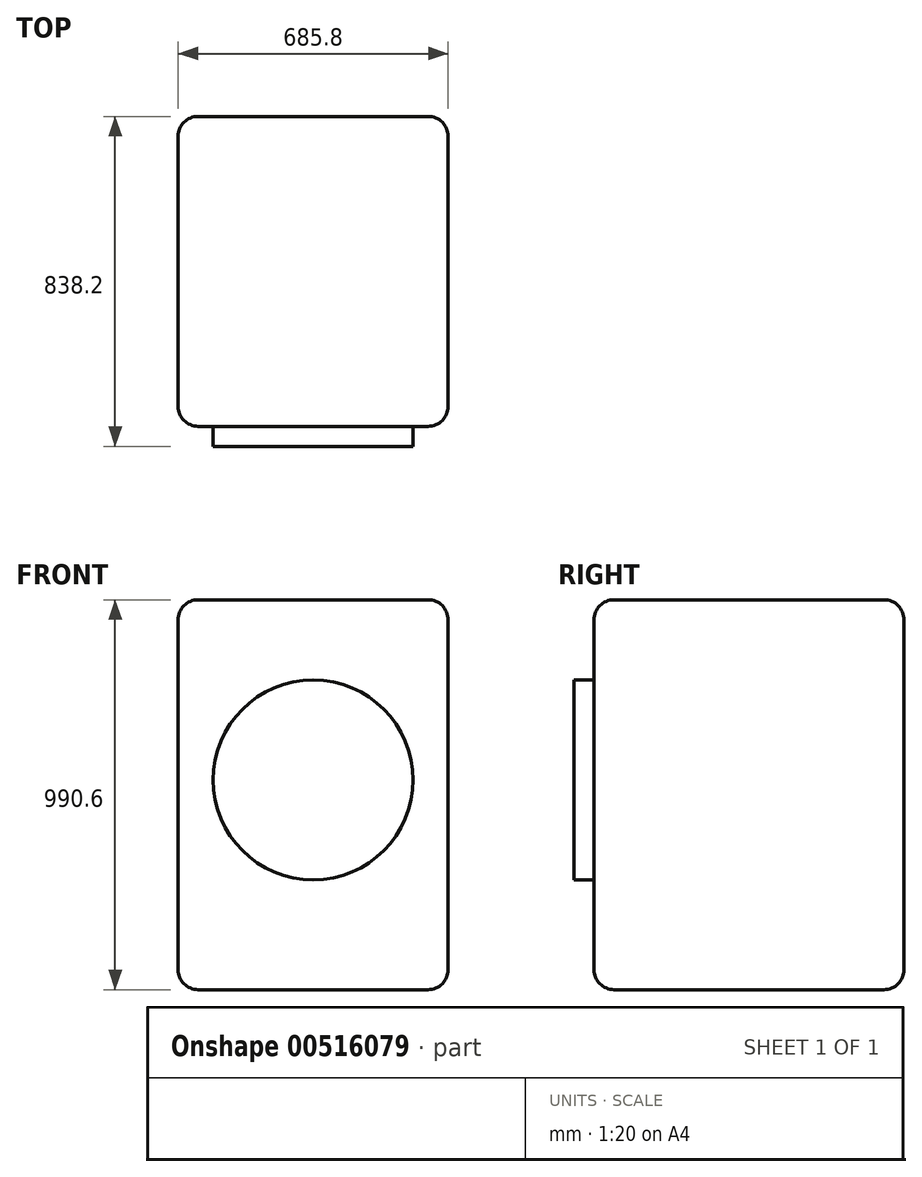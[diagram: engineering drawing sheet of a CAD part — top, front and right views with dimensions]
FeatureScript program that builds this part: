
annotation { "Feature Type Name" : "Feature", "Feature Type Description" : "" }
export const myFeature = defineFeature(function(context is Context, id is Id, definition is map)
    precondition{}
    {
        {
            var Q0;
            Q0=qCreatedBy(makeId("Top.planeOp"),FACE);
            var sketch = newSketch(context, id + "F0", { "sketchPlane" : qUnion([Q0])});
            skLineSegment(sketch, "E0.bottom", {"start": v(342.9, -393.7) * mm, "end": v(-342.9, -393.7) * mm});
            skLineSegment(sketch, "E0.top", {"start": v(342.9, 393.7) * mm, "end": v(-342.9, 393.7) * mm});
            skLineSegment(sketch, "E0.left", {"start": v(342.9, -393.7) * mm, "end": v(342.9, 393.7) * mm});
            skLineSegment(sketch, "E0.right", {"start": v(-342.9, -393.7) * mm, "end": v(-342.9, 393.7) * mm});
            skPoint(sketch, "E0.middle", {"position": v(0, 0) * mm});
            skSolve(sketch);
        }
        {
            var Q0;
            Q0=makeQuery(id+"F0.imprint","IMPRINT",FACE,{"disambiguationData":[TD([[makeQuery(id+"F0.imprint","IMPRINT",EDGE,{"derivedFrom":sQuery(id+"F0.wireOp",EDGE,"E0.bottom")}),-1.0]])]});
            extrude(context, id + "F1", {"entities" : qUnion([Q0]), "depth" : 990.6 * mm, "offsetDistance" : 25.4 * mm});
        }
        {
            var Q0;
            Q0=makeQuery(id+"F1.opExtrude","SWEPT_FACE",FACE,{"disambiguationData":[OSD([sQuery(id+"F0.wireOp",EDGE,"E0.bottom")])]});
            var sketch = newSketch(context, id + "F2", { "sketchPlane" : qUnion([Q0])});
            skCircle(sketch, "E1", {"center": v(0, 532.9) * mm, "radius": 253.93 * mm});
            skSolve(sketch);
        }
        {
            var Q0;
            Q0=makeQuery(id+"F2.imprint","IMPRINT",FACE,{"disambiguationData":[TD([[makeQuery(id+"F2.imprint","IMPRINT",EDGE,{"derivedFrom":sQuery(id+"F2.wireOp",EDGE,"E1")}),1.0]])]});
            extrude(context, id + "F3", {"entities" : qUnion([Q0]), "operationType" : NewBodyOperationType.ADD, "depth" : 50.8 * mm, "offsetDistance" : 25.4 * mm});
        }
        {
            var Q0;
            Q0=makeQuery(id+"F1.opExtrude","SWEPT_EDGE",EDGE,{"disambiguationData":[OSD([sQuery(id+"F0.wireOp",EDGE,"E0.bottom"),sQuery(id+"F0.wireOp",EDGE,"E0.right")])]});
            var Q1;
            Q1=makeQuery(id+"F1.opExtrude","CAP_EDGE",EDGE,{"disambiguationData":[OSD([sQuery(id+"F0.wireOp",EDGE,"E0.bottom")])],"isStart":false});
            var Q2;
            Q2=makeQuery(id+"F1.opExtrude","SWEPT_EDGE",EDGE,{"disambiguationData":[OSD([sQuery(id+"F0.wireOp",EDGE,"E0.bottom"),sQuery(id+"F0.wireOp",EDGE,"E0.left")])]});
            var Q3;
            Q3=makeQuery(id+"F1.opExtrude","CAP_FACE",FACE,{"disambiguationData":[OSD([sQuery(id+"F0.wireOp",EDGE,"E0.bottom"),sQuery(id+"F0.wireOp",EDGE,"E0.top"),sQuery(id+"F0.wireOp",EDGE,"E0.left"),sQuery(id+"F0.wireOp",EDGE,"E0.right")])],"isStart":false});
            var Q4;
            Q4=makeQuery(id+"F1.opExtrude","SWEPT_FACE",FACE,{"disambiguationData":[OSD([sQuery(id+"F0.wireOp",EDGE,"E0.left")])]});
            var Q5;
            Q5=makeQuery(id+"F1.opExtrude","SWEPT_FACE",FACE,{"disambiguationData":[OSD([sQuery(id+"F0.wireOp",EDGE,"E0.right")])]});
            var Q6;
            Q6=makeQuery(id+"F1.opExtrude","CAP_FACE",FACE,{"disambiguationData":[OSD([sQuery(id+"F0.wireOp",EDGE,"E0.bottom"),sQuery(id+"F0.wireOp",EDGE,"E0.top"),sQuery(id+"F0.wireOp",EDGE,"E0.left"),sQuery(id+"F0.wireOp",EDGE,"E0.right")])],"isStart":true});
            fillet(context, id + "F4", {"entities" : qUnion([Q0, Q1, Q2, Q3, Q4, Q5, Q6]), "radius" : 50.8 * mm, "tangentPropagation" : true, "allowEdgeOverflow" : false});
        }
    });
